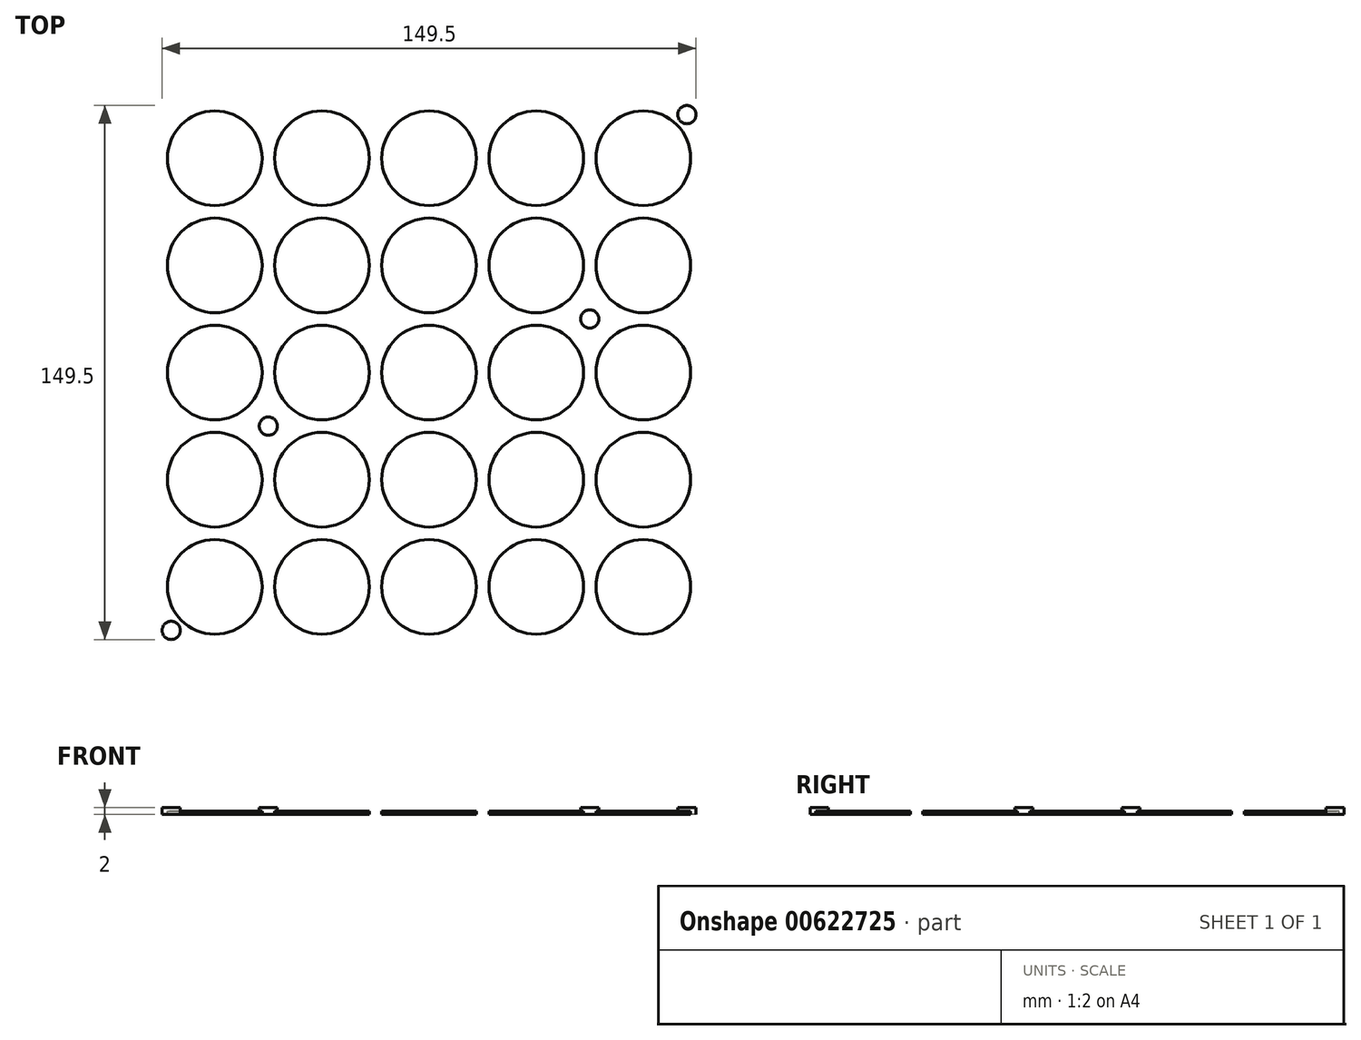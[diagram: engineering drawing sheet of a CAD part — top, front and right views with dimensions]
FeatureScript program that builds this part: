
annotation { "Feature Type Name" : "Feature", "Feature Type Description" : "" }
export const myFeature = defineFeature(function(context is Context, id is Id, definition is map)
    precondition{}
    {
        {
            var Q0;
            Q0=qCreatedBy(makeId("Top.planeOp"),FACE);
            var sketch = newSketch(context, id + "F0", { "sketchPlane" : qUnion([Q0])});
            skLineSegment(sketch, "E0.bottom", {"start": v(-76.25, 76.25) * mm, "end": v(76.25, 76.25) * mm});
            skLineSegment(sketch, "E0.top", {"start": v(-76.25, -76.25) * mm, "end": v(76.25, -76.25) * mm});
            skLineSegment(sketch, "E0.left", {"start": v(-76.25, 76.25) * mm, "end": v(-76.25, -76.25) * mm});
            skLineSegment(sketch, "E0.right", {"start": v(76.25, 76.25) * mm, "end": v(76.25, -76.25) * mm});
            skPoint(sketch, "E0.middle", {"position": v(0, 0) * mm});
            skCircle(sketch, "E1", {"center": v(-60, 60) * mm, "radius": 13.25 * mm});
            skCircle(sketch, "E2.0.1.0", {"center": v(-60, 30) * mm, "radius": 13.25 * mm});
            skCircle(sketch, "E2.0.2.0", {"center": v(-60, 0) * mm, "radius": 13.25 * mm});
            skCircle(sketch, "E2.0.3.0", {"center": v(-60, -30) * mm, "radius": 13.25 * mm});
            skCircle(sketch, "E2.0.4.0", {"center": v(-60, -60) * mm, "radius": 13.25 * mm});
            skCircle(sketch, "E2.1.0.0", {"center": v(-30, 60) * mm, "radius": 13.25 * mm});
            skCircle(sketch, "E2.1.1.0", {"center": v(-30, 30) * mm, "radius": 13.25 * mm});
            skCircle(sketch, "E2.1.2.0", {"center": v(-30, 0) * mm, "radius": 13.25 * mm});
            skCircle(sketch, "E2.1.3.0", {"center": v(-30, -30) * mm, "radius": 13.25 * mm});
            skCircle(sketch, "E2.1.4.0", {"center": v(-30, -60) * mm, "radius": 13.25 * mm});
            skCircle(sketch, "E2.2.0.0", {"center": v(0, 60) * mm, "radius": 13.25 * mm});
            skCircle(sketch, "E2.2.1.0", {"center": v(0, 30) * mm, "radius": 13.25 * mm});
            skCircle(sketch, "E2.2.2.0", {"center": v(0, 0) * mm, "radius": 13.25 * mm});
            skCircle(sketch, "E2.2.3.0", {"center": v(0, -30) * mm, "radius": 13.25 * mm});
            skCircle(sketch, "E2.2.4.0", {"center": v(0, -60) * mm, "radius": 13.25 * mm});
            skCircle(sketch, "E2.3.0.0", {"center": v(30, 60) * mm, "radius": 13.25 * mm});
            skCircle(sketch, "E2.3.1.0", {"center": v(30, 30) * mm, "radius": 13.25 * mm});
            skCircle(sketch, "E2.3.2.0", {"center": v(30, 0) * mm, "radius": 13.25 * mm});
            skCircle(sketch, "E2.3.3.0", {"center": v(30, -30) * mm, "radius": 13.25 * mm});
            skCircle(sketch, "E2.3.4.0", {"center": v(30, -60) * mm, "radius": 13.25 * mm});
            skCircle(sketch, "E2.4.0.0", {"center": v(60, 60) * mm, "radius": 13.25 * mm});
            skCircle(sketch, "E2.4.1.0", {"center": v(60, 30) * mm, "radius": 13.25 * mm});
            skCircle(sketch, "E2.4.2.0", {"center": v(60, 0) * mm, "radius": 13.25 * mm});
            skCircle(sketch, "E2.4.3.0", {"center": v(60, -30) * mm, "radius": 13.25 * mm});
            skCircle(sketch, "E2.4.4.0", {"center": v(60, -60) * mm, "radius": 13.25 * mm});
            skLineSegment(sketch, "E2.direction1", {"start": v(-60, 60) * mm, "end": v(-30, 60) * mm, "construction": true});
            skLineSegment(sketch, "E2.direction2", {"start": v(-60, 60) * mm, "end": v(-60, 30) * mm, "construction": true});
            skSolve(sketch);
        }
        {
            var Q0;
            Q0=makeQuery(id+"F0.imprint","IMPRINT",FACE,{"disambiguationData":[TD([[makeQuery(id+"F0.imprint","IMPRINT",EDGE,{"derivedFrom":sQuery(id+"F0.wireOp",EDGE,"E1")}),1.0]])]});
            var Q1;
            Q1=makeQuery(id+"F0.imprint","IMPRINT",FACE,{"disambiguationData":[TD([[makeQuery(id+"F0.imprint","IMPRINT",EDGE,{"derivedFrom":sQuery(id+"F0.wireOp",EDGE,"E2.1.0.0")}),1.0]])]});
            var Q2;
            Q2=makeQuery(id+"F0.imprint","IMPRINT",FACE,{"disambiguationData":[TD([[makeQuery(id+"F0.imprint","IMPRINT",EDGE,{"derivedFrom":sQuery(id+"F0.wireOp",EDGE,"E2.2.0.0")}),1.0]])]});
            var Q3;
            Q3=makeQuery(id+"F0.imprint","IMPRINT",FACE,{"disambiguationData":[TD([[makeQuery(id+"F0.imprint","IMPRINT",EDGE,{"derivedFrom":sQuery(id+"F0.wireOp",EDGE,"E2.3.0.0")}),1.0]])]});
            var Q4;
            Q4=makeQuery(id+"F0.imprint","IMPRINT",FACE,{"disambiguationData":[TD([[makeQuery(id+"F0.imprint","IMPRINT",EDGE,{"derivedFrom":sQuery(id+"F0.wireOp",EDGE,"E2.4.0.0")}),1.0]])]});
            var Q5;
            Q5=makeQuery(id+"F0.imprint","IMPRINT",FACE,{"disambiguationData":[TD([[makeQuery(id+"F0.imprint","IMPRINT",EDGE,{"derivedFrom":sQuery(id+"F0.wireOp",EDGE,"E2.4.1.0")}),1.0]])]});
            var Q6;
            Q6=makeQuery(id+"F0.imprint","IMPRINT",FACE,{"disambiguationData":[TD([[makeQuery(id+"F0.imprint","IMPRINT",EDGE,{"derivedFrom":sQuery(id+"F0.wireOp",EDGE,"E2.3.1.0")}),1.0]])]});
            var Q7;
            Q7=makeQuery(id+"F0.imprint","IMPRINT",FACE,{"disambiguationData":[TD([[makeQuery(id+"F0.imprint","IMPRINT",EDGE,{"derivedFrom":sQuery(id+"F0.wireOp",EDGE,"E0.bottom")}),-1.0]])]});
            var Q8;
            Q8=makeQuery(id+"F0.imprint","IMPRINT",FACE,{"disambiguationData":[TD([[makeQuery(id+"F0.imprint","IMPRINT",EDGE,{"derivedFrom":sQuery(id+"F0.wireOp",EDGE,"E2.1.1.0")}),1.0]])]});
            var Q9;
            Q9=makeQuery(id+"F0.imprint","IMPRINT",FACE,{"disambiguationData":[TD([[makeQuery(id+"F0.imprint","IMPRINT",EDGE,{"derivedFrom":sQuery(id+"F0.wireOp",EDGE,"E2.0.1.0")}),1.0]])]});
            var Q10;
            Q10=makeQuery(id+"F0.imprint","IMPRINT",FACE,{"disambiguationData":[TD([[makeQuery(id+"F0.imprint","IMPRINT",EDGE,{"derivedFrom":sQuery(id+"F0.wireOp",EDGE,"E2.2.1.0")}),1.0]])]});
            var Q11;
            Q11=makeQuery(id+"F0.imprint","IMPRINT",FACE,{"disambiguationData":[TD([[makeQuery(id+"F0.imprint","IMPRINT",EDGE,{"derivedFrom":sQuery(id+"F0.wireOp",EDGE,"E2.2.2.0")}),1.0]])]});
            var Q12;
            Q12=makeQuery(id+"F0.imprint","IMPRINT",FACE,{"disambiguationData":[TD([[makeQuery(id+"F0.imprint","IMPRINT",EDGE,{"derivedFrom":sQuery(id+"F0.wireOp",EDGE,"E2.1.2.0")}),1.0]])]});
            var Q13;
            Q13=makeQuery(id+"F0.imprint","IMPRINT",FACE,{"disambiguationData":[TD([[makeQuery(id+"F0.imprint","IMPRINT",EDGE,{"derivedFrom":sQuery(id+"F0.wireOp",EDGE,"E2.0.2.0")}),1.0]])]});
            var Q14;
            Q14=makeQuery(id+"F0.imprint","IMPRINT",FACE,{"disambiguationData":[TD([[makeQuery(id+"F0.imprint","IMPRINT",EDGE,{"derivedFrom":sQuery(id+"F0.wireOp",EDGE,"E2.3.2.0")}),1.0]])]});
            var Q15;
            Q15=makeQuery(id+"F0.imprint","IMPRINT",FACE,{"disambiguationData":[TD([[makeQuery(id+"F0.imprint","IMPRINT",EDGE,{"derivedFrom":sQuery(id+"F0.wireOp",EDGE,"E2.4.2.0")}),1.0]])]});
            var Q16;
            Q16=makeQuery(id+"F0.imprint","IMPRINT",FACE,{"disambiguationData":[TD([[makeQuery(id+"F0.imprint","IMPRINT",EDGE,{"derivedFrom":sQuery(id+"F0.wireOp",EDGE,"E2.3.3.0")}),1.0]])]});
            var Q17;
            Q17=makeQuery(id+"F0.imprint","IMPRINT",FACE,{"disambiguationData":[TD([[makeQuery(id+"F0.imprint","IMPRINT",EDGE,{"derivedFrom":sQuery(id+"F0.wireOp",EDGE,"E2.4.3.0")}),1.0]])]});
            var Q18;
            Q18=makeQuery(id+"F0.imprint","IMPRINT",FACE,{"disambiguationData":[TD([[makeQuery(id+"F0.imprint","IMPRINT",EDGE,{"derivedFrom":sQuery(id+"F0.wireOp",EDGE,"E2.4.4.0")}),1.0]])]});
            var Q19;
            Q19=makeQuery(id+"F0.imprint","IMPRINT",FACE,{"disambiguationData":[TD([[makeQuery(id+"F0.imprint","IMPRINT",EDGE,{"derivedFrom":sQuery(id+"F0.wireOp",EDGE,"E2.3.4.0")}),1.0]])]});
            var Q20;
            Q20=makeQuery(id+"F0.imprint","IMPRINT",FACE,{"disambiguationData":[TD([[makeQuery(id+"F0.imprint","IMPRINT",EDGE,{"derivedFrom":sQuery(id+"F0.wireOp",EDGE,"E2.2.4.0")}),1.0]])]});
            var Q21;
            Q21=makeQuery(id+"F0.imprint","IMPRINT",FACE,{"disambiguationData":[TD([[makeQuery(id+"F0.imprint","IMPRINT",EDGE,{"derivedFrom":sQuery(id+"F0.wireOp",EDGE,"E2.2.3.0")}),1.0]])]});
            var Q22;
            Q22=makeQuery(id+"F0.imprint","IMPRINT",FACE,{"disambiguationData":[TD([[makeQuery(id+"F0.imprint","IMPRINT",EDGE,{"derivedFrom":sQuery(id+"F0.wireOp",EDGE,"E2.1.4.0")}),1.0]])]});
            var Q23;
            Q23=makeQuery(id+"F0.imprint","IMPRINT",FACE,{"disambiguationData":[TD([[makeQuery(id+"F0.imprint","IMPRINT",EDGE,{"derivedFrom":sQuery(id+"F0.wireOp",EDGE,"E2.1.3.0")}),1.0]])]});
            var Q24;
            Q24=makeQuery(id+"F0.imprint","IMPRINT",FACE,{"disambiguationData":[TD([[makeQuery(id+"F0.imprint","IMPRINT",EDGE,{"derivedFrom":sQuery(id+"F0.wireOp",EDGE,"E2.0.3.0")}),1.0]])]});
            var Q25;
            Q25=makeQuery(id+"F0.imprint","IMPRINT",FACE,{"disambiguationData":[TD([[makeQuery(id+"F0.imprint","IMPRINT",EDGE,{"derivedFrom":sQuery(id+"F0.wireOp",EDGE,"E2.0.4.0")}),1.0]])]});
            extrude(context, id + "F1", {"entities" : qUnion([Q0, Q1, Q2, Q3, Q4, Q5, Q6, Q7, Q8, Q9, Q10, Q11, Q12, Q13, Q14, Q15, Q16, Q17, Q18, Q19, Q20, Q21, Q22, Q23, Q24, Q25]), "depth" : 1 * mm, "offsetDistance" : 25 * mm});
        }
        {
            var Q0;
            Q0 = qSketchRegion(id + "F0", true);
            extrude(context, id + "F2", {"entities" : qUnion([Q0]), "operationType" : NewBodyOperationType.ADD, "depth" : 2 * mm, "offsetDistance" : 25 * mm});
        }
        {
            var Q0;
            Q0=makeQuery(id+"F2.opExtrude","CAP_FACE",FACE,{"disambiguationData":[OSD([sQuery(id+"F0.wireOp",EDGE,"E0.bottom"),sQuery(id+"F0.wireOp",EDGE,"E0.top"),sQuery(id+"F0.wireOp",EDGE,"E0.left"),sQuery(id+"F0.wireOp",EDGE,"E0.right"),sQuery(id+"F0.wireOp",EDGE,"E1"),sQuery(id+"F0.wireOp",EDGE,"E2.0.1.0"),sQuery(id+"F0.wireOp",EDGE,"E2.0.2.0"),sQuery(id+"F0.wireOp",EDGE,"E2.0.3.0"),sQuery(id+"F0.wireOp",EDGE,"E2.0.4.0"),sQuery(id+"F0.wireOp",EDGE,"E2.1.0.0"),sQuery(id+"F0.wireOp",EDGE,"E2.1.1.0"),sQuery(id+"F0.wireOp",EDGE,"E2.1.2.0"),sQuery(id+"F0.wireOp",EDGE,"E2.1.3.0"),sQuery(id+"F0.wireOp",EDGE,"E2.1.4.0"),sQuery(id+"F0.wireOp",EDGE,"E2.2.0.0"),sQuery(id+"F0.wireOp",EDGE,"E2.2.1.0"),sQuery(id+"F0.wireOp",EDGE,"E2.2.2.0"),sQuery(id+"F0.wireOp",EDGE,"E2.2.3.0"),sQuery(id+"F0.wireOp",EDGE,"E2.2.4.0"),sQuery(id+"F0.wireOp",EDGE,"E2.3.0.0"),sQuery(id+"F0.wireOp",EDGE,"E2.3.1.0"),sQuery(id+"F0.wireOp",EDGE,"E2.3.2.0"),sQuery(id+"F0.wireOp",EDGE,"E2.3.3.0"),sQuery(id+"F0.wireOp",EDGE,"E2.3.4.0"),sQuery(id+"F0.wireOp",EDGE,"E2.4.0.0"),sQuery(id+"F0.wireOp",EDGE,"E2.4.1.0"),sQuery(id+"F0.wireOp",EDGE,"E2.4.2.0"),sQuery(id+"F0.wireOp",EDGE,"E2.4.3.0"),sQuery(id+"F0.wireOp",EDGE,"E2.4.4.0")])],"isStart":false});
            var sketch = newSketch(context, id + "F3", { "sketchPlane" : qUnion([Q0])});
            skLineSegment(sketch, "E3", {"start": v(0, 74.2) * mm, "end": v(0, -73.43) * mm, "construction": true});
            skLineSegment(sketch, "E4", {"start": v(-81.9, 0) * mm, "end": v(78.5, 0) * mm, "construction": true});
            skCircle(sketch, "E5", {"center": v(-72.2, 72.2) * mm, "radius": 2.55 * mm});
            skCircle(sketch, "E6", {"center": v(-45, 15) * mm, "radius": 2.55 * mm});
            skCircle(sketch, "E7.MirrorC", {"center": v(72.2, 72.2) * mm, "radius": 2.55 * mm});
            skCircle(sketch, "E8.MirrorC", {"center": v(45, 15) * mm, "radius": 2.55 * mm});
            skCircle(sketch, "E9.MirrorC", {"center": v(-45, -15) * mm, "radius": 2.55 * mm});
            skCircle(sketch, "E10.MirrorC", {"center": v(45, -15) * mm, "radius": 2.55 * mm});
            skCircle(sketch, "E11.MirrorC", {"center": v(72.2, -72.2) * mm, "radius": 2.55 * mm});
            skCircle(sketch, "E12.MirrorC", {"center": v(-72.2, -72.2) * mm, "radius": 2.55 * mm});
            skSolve(sketch);
        }
        {
            var Q0;
            Q0=makeQuery(id+"F3.imprint","IMPRINT",FACE,{"disambiguationData":[TD([[makeQuery(id+"F3.imprint","IMPRINT",EDGE,{"derivedFrom":sQuery(id+"F3.wireOp",EDGE,"E5")}),1.0]])]});
            var Q1;
            Q1=makeQuery(id+"F3.imprint","IMPRINT",FACE,{"disambiguationData":[TD([[makeQuery(id+"F3.imprint","IMPRINT",EDGE,{"derivedFrom":sQuery(id+"F3.wireOp",EDGE,"E7.MirrorC")}),-1.0]])]});
            var Q2;
            Q2=makeQuery(id+"F3.imprint","IMPRINT",FACE,{"disambiguationData":[TD([[makeQuery(id+"F3.imprint","IMPRINT",EDGE,{"derivedFrom":sQuery(id+"F3.wireOp",EDGE,"E8.MirrorC")}),-1.0]])]});
            var Q3;
            Q3=makeQuery(id+"F3.imprint","IMPRINT",FACE,{"disambiguationData":[TD([[makeQuery(id+"F3.imprint","IMPRINT",EDGE,{"derivedFrom":sQuery(id+"F3.wireOp",EDGE,"E6")}),1.0]])]});
            var Q4;
            Q4=makeQuery(id+"F3.imprint","IMPRINT",FACE,{"disambiguationData":[TD([[makeQuery(id+"F3.imprint","IMPRINT",EDGE,{"derivedFrom":sQuery(id+"F3.wireOp",EDGE,"E10.MirrorC")}),1.0]])]});
            var Q5;
            Q5=makeQuery(id+"F3.imprint","IMPRINT",FACE,{"disambiguationData":[TD([[makeQuery(id+"F3.imprint","IMPRINT",EDGE,{"derivedFrom":sQuery(id+"F3.wireOp",EDGE,"E9.MirrorC")}),-1.0]])]});
            var Q6;
            Q6=makeQuery(id+"F3.imprint","IMPRINT",FACE,{"disambiguationData":[TD([[makeQuery(id+"F3.imprint","IMPRINT",EDGE,{"derivedFrom":sQuery(id+"F3.wireOp",EDGE,"E12.MirrorC")}),-1.0]])]});
            var Q7;
            Q7=makeQuery(id+"F3.imprint","IMPRINT",FACE,{"disambiguationData":[TD([[makeQuery(id+"F3.imprint","IMPRINT",EDGE,{"derivedFrom":sQuery(id+"F3.wireOp",EDGE,"E11.MirrorC")}),1.0]])]});
            extrude(context, id + "F4", {"entities" : qUnion([Q0, Q1, Q2, Q3, Q4, Q5, Q6, Q7]), "operationType" : NewBodyOperationType.REMOVE, "endBound" : BoundingType.THROUGH_ALL, "oppositeDirection" : true, "depth" : 25 * mm, "offsetDistance" : 25 * mm});
        }
    });
